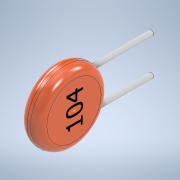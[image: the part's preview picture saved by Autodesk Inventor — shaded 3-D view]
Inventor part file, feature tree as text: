
AUTODESK INVENTOR PART (.ipt)
format: ipt  version: 2020 (Build 240168000, 168)  size: 165,888 bytes
history: native  units: mm
features: sketch x4, projected_geometry x3, extrude x2, fillet x2, other x1, plane x1
ambient origin geometry x8: Origin, YZ Plane, XZ Plane, XY Plane, X Axis, Y Axis, Z Axis, Center Point
bodies: Body1 (feature_tree)
feature tree (13):
  other  "Sólido1"
  extrude  "Extrusión1"  Depth=0.5mm TaperAngle=0.0deg
  fillet  "Empalme1"  Radius=0.5mm
  fillet  "Empalme2"  Radius=0.5mm
  sketch  "Boceto2"  dims[d5=-1.3mm d7=0.3mm]
  sketch  "Boceto3"  dims[d8=0.3mm]
  plane  "Plano de trabajo1"
  extrude  "Extrusión2"  Depth=0.3mm
  sketch  "Boceto1"  dims[d0=4.3mm d1=1.2mm d2=0.0mm d3=0.5mm d4=0.5mm]
  sketch  "Boceto4"  dims[d9=4.0mm d10=0.0mm]
  projected_geometry  "Contorno proyectado1"
  projected_geometry  "Contorno proyectado2"
  projected_geometry  "Contorno proyectado3"
